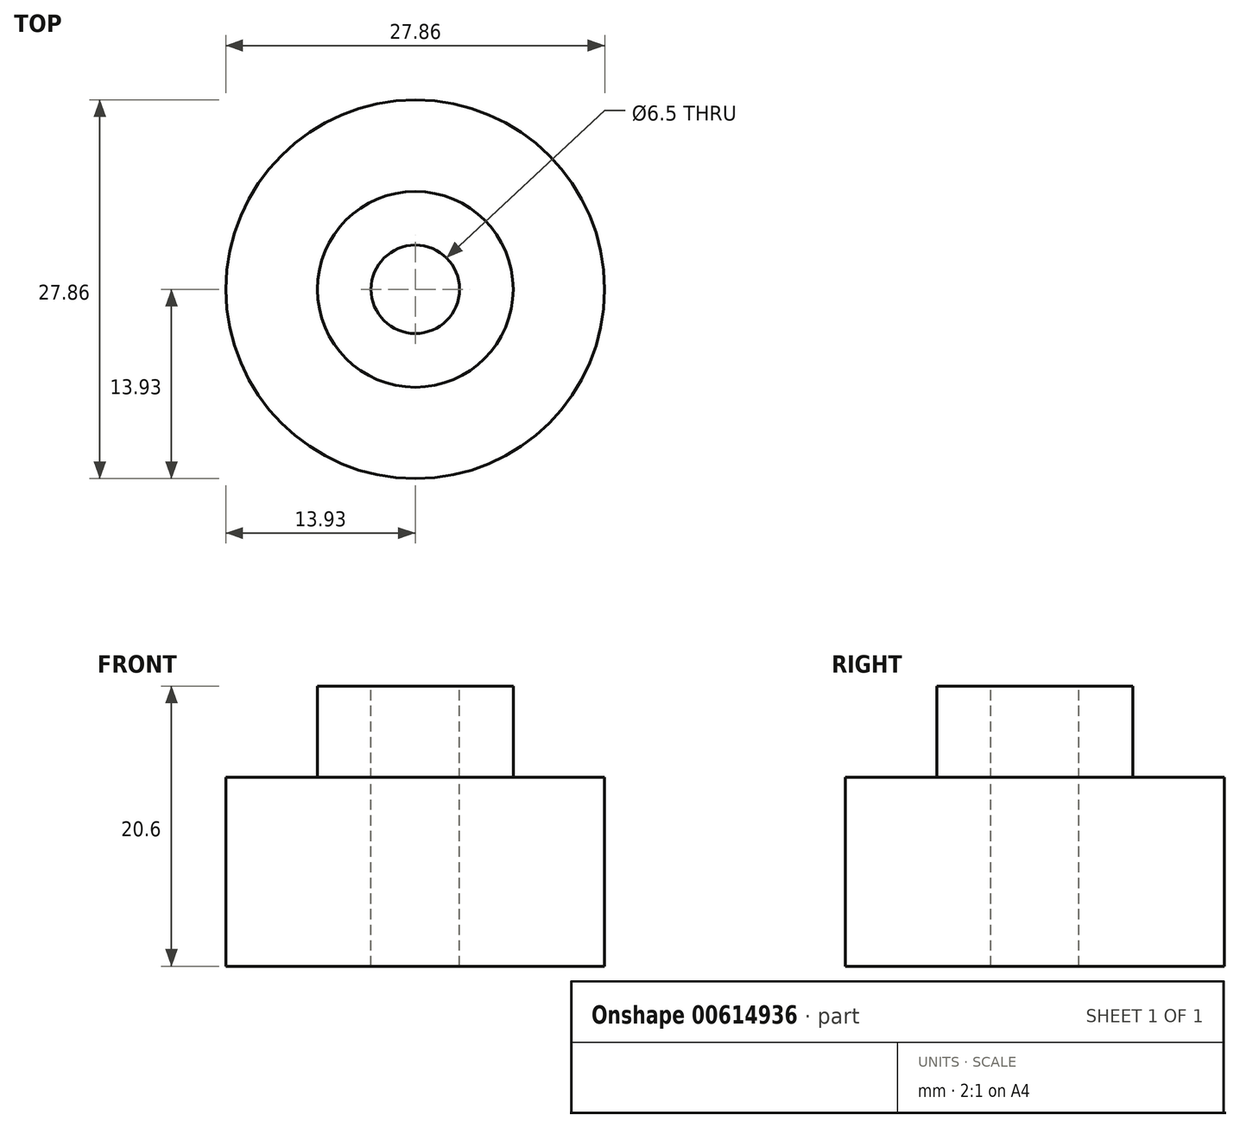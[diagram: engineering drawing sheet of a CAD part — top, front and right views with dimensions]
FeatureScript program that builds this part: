
annotation { "Feature Type Name" : "Feature", "Feature Type Description" : "" }
export const myFeature = defineFeature(function(context is Context, id is Id, definition is map)
    precondition{}
    {
        {
            var Q0;
            Q0=qCreatedBy(makeId("Top.planeOp"),FACE);
            var sketch = newSketch(context, id + "F0", { "sketchPlane" : qUnion([Q0])});
            skCircle(sketch, "E0", {"center": v(0, 0) * mm, "radius": 13.93 * mm});
            skSolve(sketch);
        }
        {
            var Q0;
            Q0 = qSketchRegion(id + "F0", true);
            extrude(context, id + "F1", {"entities" : qUnion([Q0]), "depth" : 13.9 * mm, "offsetDistance" : 25 * mm});
        }
        {
            var Q0;
            Q0=makeQuery(id+"F1.opExtrude","CAP_FACE",FACE,{"disambiguationData":[OSD([sQuery(id+"F0.wireOp",EDGE,"E0")])],"isStart":false});
            var sketch = newSketch(context, id + "F2", { "sketchPlane" : qUnion([Q0])});
            skCircle(sketch, "E1", {"center": v(0, 0) * mm, "radius": 7.2 * mm});
            skSolve(sketch);
        }
        {
            var Q0;
            Q0 = qSketchRegion(id + "F2", true);
            extrude(context, id + "F3", {"entities" : qUnion([Q0]), "operationType" : NewBodyOperationType.ADD, "depth" : 6.7 * mm, "offsetDistance" : 25 * mm});
        }
        {
            var Q0;
            Q0=makeQuery(id+"F3.opExtrude","CAP_FACE",FACE,{"disambiguationData":[OSD([sQuery(id+"F2.wireOp",EDGE,"E1")])],"isStart":false});
            var sketch = newSketch(context, id + "F4", { "sketchPlane" : qUnion([Q0])});
            skCircle(sketch, "E2", {"center": v(0, 0) * mm, "radius": 3.25 * mm});
            skSolve(sketch);
        }
        {
            var Q0;
            Q0=makeQuery(id+"F4.imprint","IMPRINT",FACE,{"disambiguationData":[TD([[makeQuery(id+"F4.imprint","IMPRINT",EDGE,{"derivedFrom":sQuery(id+"F4.wireOp",EDGE,"E2")}),1.0]])]});
            extrude(context, id + "F5", {"entities" : qUnion([Q0]), "operationType" : NewBodyOperationType.REMOVE, "oppositeDirection" : true, "depth" : 352.2 * mm, "offsetDistance" : 25 * mm});
        }
    });
